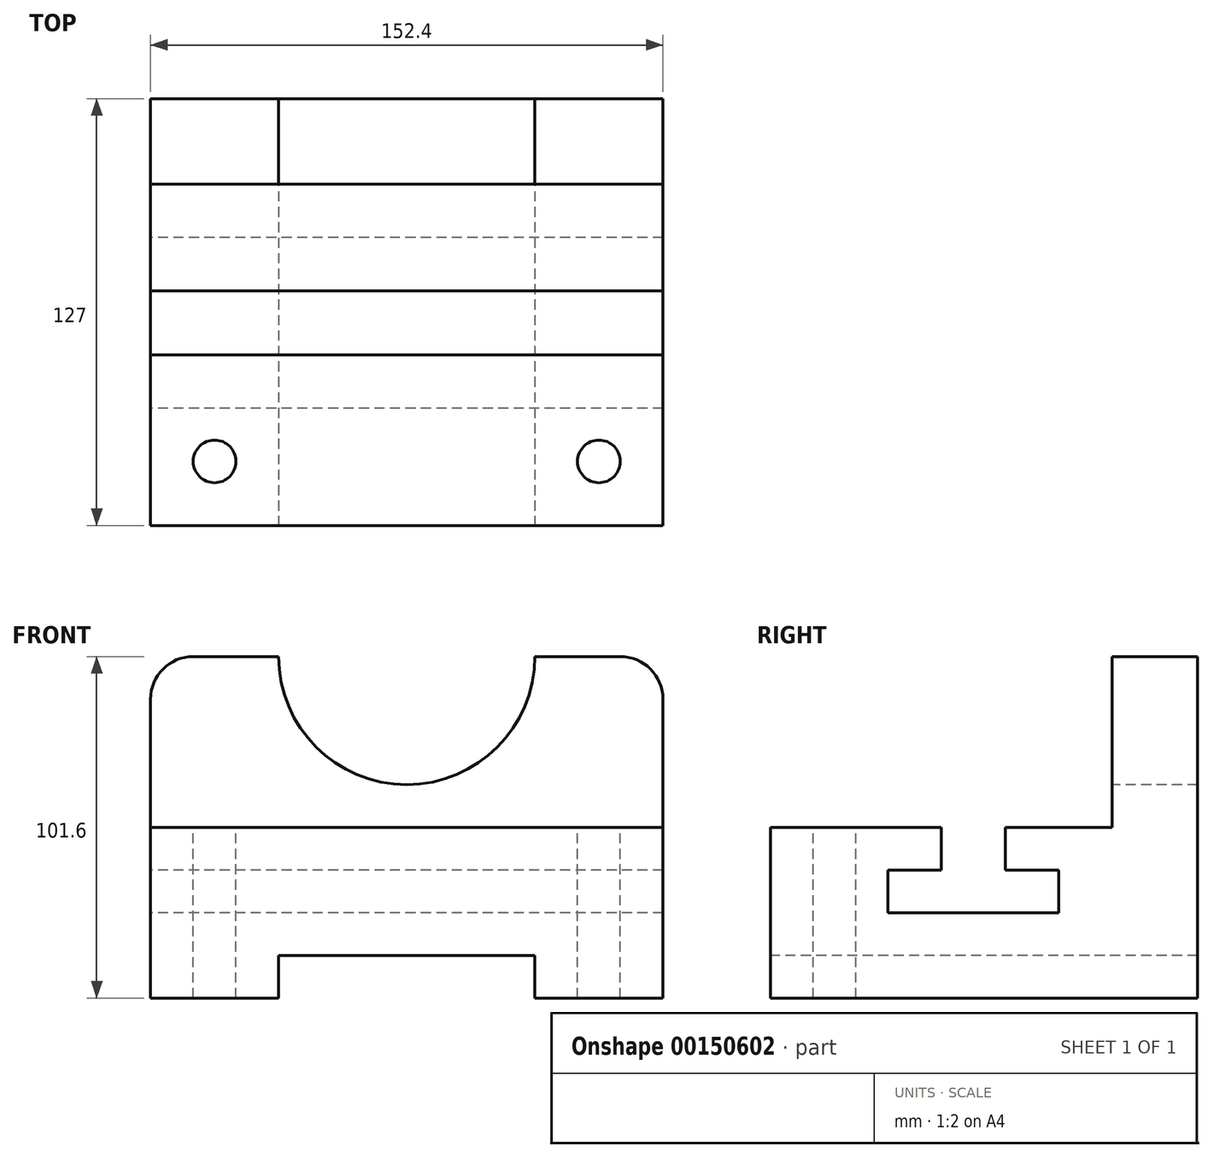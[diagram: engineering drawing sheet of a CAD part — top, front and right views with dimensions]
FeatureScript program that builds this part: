
annotation { "Feature Type Name" : "Feature", "Feature Type Description" : "" }
export const myFeature = defineFeature(function(context is Context, id is Id, definition is map)
    precondition{}
    {
        {
            var Q0;
            Q0=qCreatedBy(makeId("Right.planeOp"),FACE);
            var sketch = newSketch(context, id + "F0", { "sketchPlane" : qUnion([Q0])});
            skLineSegment(sketch, "E0", {"start": v(0, 0) * mm, "end": v(127, 0) * mm});
            skLineSegment(sketch, "E1", {"start": v(0, 0) * mm, "end": v(0, 50.8) * mm});
            skLineSegment(sketch, "E2", {"start": v(0, 50.8) * mm, "end": v(50.8, 50.8) * mm});
            skLineSegment(sketch, "E3", {"start": v(101.6, 50.8) * mm, "end": v(101.6, 101.6) * mm});
            skLineSegment(sketch, "E4", {"start": v(101.6, 101.6) * mm, "end": v(127, 101.6) * mm});
            skLineSegment(sketch, "E5", {"start": v(127, 101.6) * mm, "end": v(127, 0) * mm});
            skLineSegment(sketch, "E6", {"start": v(50.8, 50.8) * mm, "end": v(50.8, 38.1) * mm});
            skLineSegment(sketch, "E7", {"start": v(50.8, 38.1) * mm, "end": v(34.92, 38.1) * mm});
            skLineSegment(sketch, "E8", {"start": v(34.92, 38.1) * mm, "end": v(34.92, 25.4) * mm});
            skLineSegment(sketch, "E9", {"start": v(34.92, 25.4) * mm, "end": v(85.72, 25.4) * mm});
            skLineSegment(sketch, "E10", {"start": v(85.72, 25.4) * mm, "end": v(85.72, 38.1) * mm});
            skLineSegment(sketch, "E11", {"start": v(85.72, 38.1) * mm, "end": v(69.85, 38.1) * mm});
            skLineSegment(sketch, "E12", {"start": v(69.85, 38.1) * mm, "end": v(69.85, 50.8) * mm});
            skLineSegment(sketch, "E13.trimOffspring", {"start": v(69.85, 50.8) * mm, "end": v(101.6, 50.8) * mm});
            skSolve(sketch);
        }
        {
            var Q0;
            Q0=makeQuery(id+"F0.imprint","IMPRINT",FACE,{"disambiguationData":[TD([[makeQuery(id+"F0.imprint","IMPRINT",EDGE,{"derivedFrom":sQuery(id+"F0.wireOp",EDGE,"E0")}),1.0]])]});
            extrude(context, id + "F1", {"entities" : qUnion([Q0]), "depth" : 152.4 * mm});
        }
        {
            var Q0;
            Q0=qCreatedBy(makeId("Front.planeOp"),FACE);
            var sketch = newSketch(context, id + "F2", { "sketchPlane" : qUnion([Q0])});
            skLineSegment(sketch, "E14.0", {"start": v(152.4, 0) * mm, "end": v(0, 0) * mm});
            skLineSegment(sketch, "E15.0", {"start": v(152.4, 50.8) * mm, "end": v(0, 50.8) * mm});
            skPoint(sketch, "E16.0", {"position": v(0, 38.1) * mm});
            skPoint(sketch, "E17.0", {"position": v(152.4, 38.1) * mm});
            skLineSegment(sketch, "E18.0", {"start": v(152.4, 0) * mm, "end": v(152.4, 50.8) * mm});
            skLineSegment(sketch, "E19.0", {"start": v(0, 0) * mm, "end": v(0, 50.8) * mm});
            skLineSegment(sketch, "E20", {"start": v(38.1, 0) * mm, "end": v(38.1, 12.7) * mm});
            skLineSegment(sketch, "E21", {"start": v(38.1, 12.7) * mm, "end": v(114.3, 12.7) * mm});
            skLineSegment(sketch, "E22", {"start": v(114.3, 12.7) * mm, "end": v(114.3, 0) * mm});
            skSolve(sketch);
        }
        {
            var Q0;
            {var subQ0=sQuery(id+"F2.wireOp",EDGE,"E20");Q0=makeQuery(id+"F2.imprint","IMPRINT",FACE,{"disambiguationData":[TD([[makeQuery(id+"F2.imprint","IMPRINT",EDGE,{"derivedFrom":subQ0}),-1.0]])]});}
            extrude(context, id + "F3", {"entities" : qUnion([Q0]), "operationType" : NewBodyOperationType.REMOVE, "oppositeDirection" : true, "depth" : 152.4 * mm});
        }
        {
            var Q0;
            Q0=qCreatedBy(makeId("Front.planeOp"),FACE);
            var sketch = newSketch(context, id + "F4", { "sketchPlane" : qUnion([Q0])});
            skLineSegment(sketch, "E23.0", {"start": v(152.4, 101.6) * mm, "end": v(0, 101.6) * mm});
            skLineSegment(sketch, "E24.0", {"start": v(152.4, 101.6) * mm, "end": v(152.4, 0) * mm});
            skLineSegment(sketch, "E25.0", {"start": v(0, 101.6) * mm, "end": v(0, 0) * mm});
            skArc(sketch, "E26", {"start": v(38.1, 101.6) * mm, "mid": v(76.2, 63.5) * mm, "end": v(114.3, 101.6) * mm});
            skSolve(sketch);
        }
        {
            var Q0;
            Q0 = qSketchRegion(id + "F4", true);
            extrude(context, id + "F5", {"entities" : qUnion([Q0]), "operationType" : NewBodyOperationType.REMOVE, "oppositeDirection" : true, "depth" : 149.22 * mm});
        }
        {
            var Q0;
            Q0=makeQuery(id+"F1.opExtrude","CAP_EDGE",EDGE,{"disambiguationData":[OSD([sQuery(id+"F0.wireOp",EDGE,"E4")])],"isStart":false});
            var Q1;
            Q1=makeQuery(id+"F1.opExtrude","CAP_EDGE",EDGE,{"disambiguationData":[OSD([sQuery(id+"F0.wireOp",EDGE,"E4")])],"isStart":true});
            fillet(context, id + "F6", {"entities" : qUnion([Q0, Q1]), "radius" : 12.7 * mm, "tangentPropagation" : true, "allowEdgeOverflow" : false});
        }
        {
            var Q0;
            Q0=makeQuery(id+"F1.opExtrude","SWEPT_FACE",FACE,{"disambiguationData":[OSD([sQuery(id+"F0.wireOp",EDGE,"E2")])]});
            var sketch = newSketch(context, id + "F7", { "sketchPlane" : qUnion([Q0])});
            skCircle(sketch, "E27", {"center": v(19.05, 19.05) * mm, "radius": 6.35 * mm});
            skCircle(sketch, "E28", {"center": v(133.35, 19.05) * mm, "radius": 6.35 * mm});
            skSolve(sketch);
        }
        {
            var Q0;
            Q0=makeQuery(id+"F7.imprint","IMPRINT",FACE,{"disambiguationData":[TD([[makeQuery(id+"F7.imprint","IMPRINT",EDGE,{"derivedFrom":sQuery(id+"F7.wireOp",EDGE,"E27")}),1.0]])]});
            var Q1;
            Q1=makeQuery(id+"F7.imprint","IMPRINT",FACE,{"disambiguationData":[TD([[makeQuery(id+"F7.imprint","IMPRINT",EDGE,{"derivedFrom":sQuery(id+"F7.wireOp",EDGE,"E28")}),1.0]])]});
            extrude(context, id + "F8", {"entities" : qUnion([Q0, Q1]), "operationType" : NewBodyOperationType.REMOVE, "oppositeDirection" : true, "depth" : 80.64 * mm});
        }
    });
